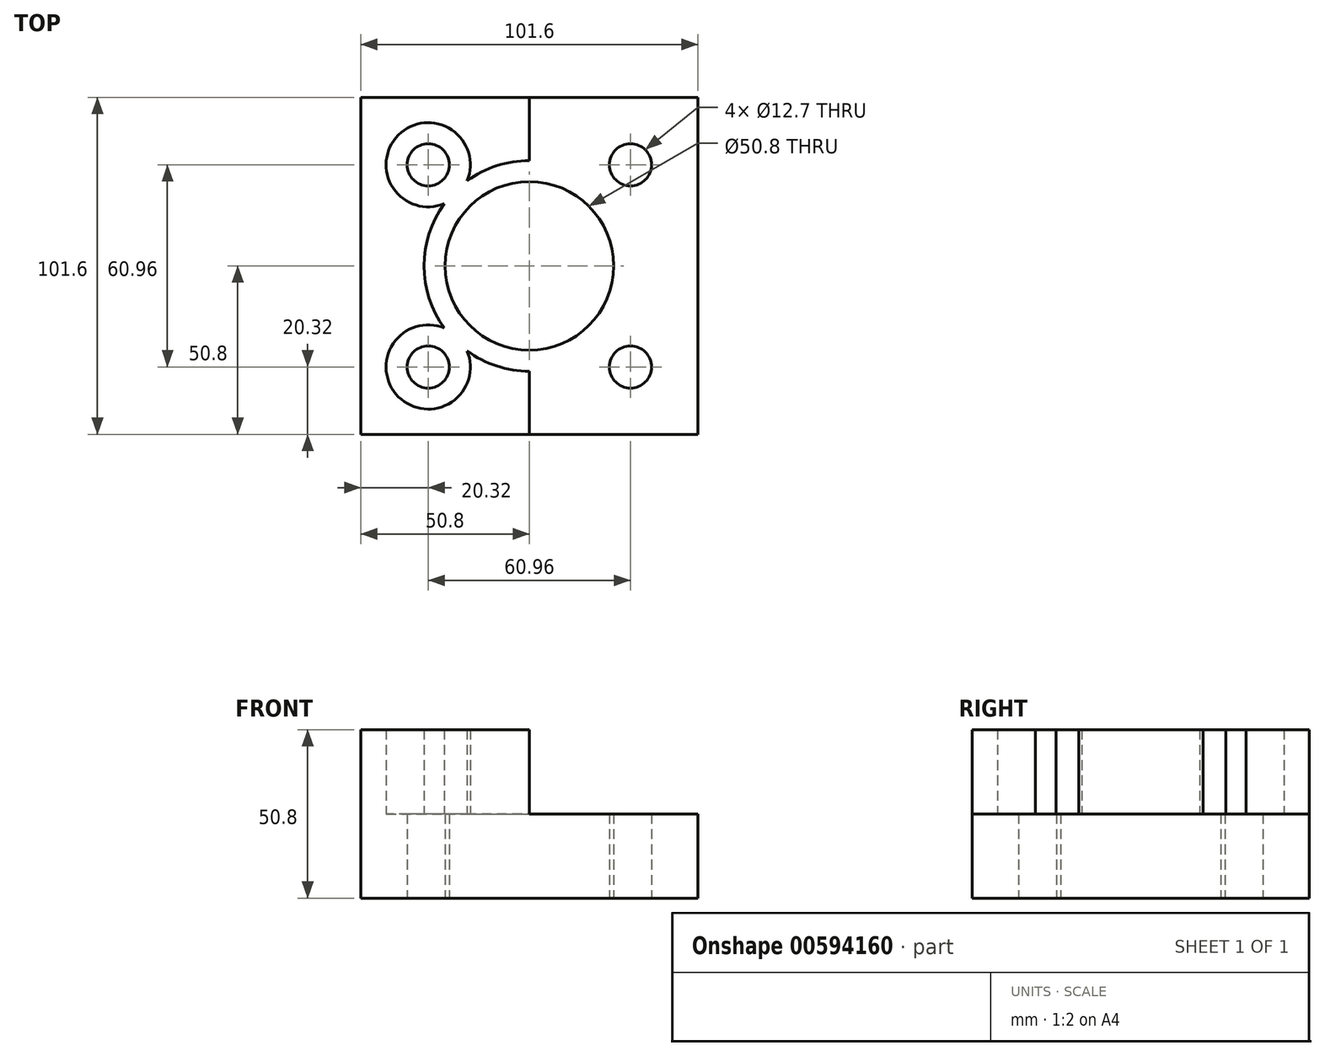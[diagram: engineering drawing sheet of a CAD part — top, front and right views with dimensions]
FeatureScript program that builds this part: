
annotation { "Feature Type Name" : "Feature", "Feature Type Description" : "" }
export const myFeature = defineFeature(function(context is Context, id is Id, definition is map)
    precondition{}
    {
        {
            var Q0;
            Q0=qCreatedBy(makeId("Top.planeOp"),FACE);
            var sketch = newSketch(context, id + "F0", { "sketchPlane" : qUnion([Q0])});
            skCircle(sketch, "E0", {"center": v(0, 0) * mm, "radius": 25.4 * mm});
            skLineSegment(sketch, "E1.bottom", {"start": v(-50.8, 50.8) * mm, "end": v(50.8, 50.8) * mm});
            skLineSegment(sketch, "E1.top", {"start": v(-50.8, -50.8) * mm, "end": v(50.8, -50.8) * mm});
            skLineSegment(sketch, "E1.left", {"start": v(-50.8, 50.8) * mm, "end": v(-50.8, -50.8) * mm});
            skLineSegment(sketch, "E1.right", {"start": v(50.8, 50.8) * mm, "end": v(50.8, -50.8) * mm});
            skCircle(sketch, "E2", {"center": v(-30.48, -30.48) * mm, "radius": 6.35 * mm});
            skCircle(sketch, "E3.1.0", {"center": v(30.48, -30.48) * mm, "radius": 6.35 * mm});
            skCircle(sketch, "E3.2.0", {"center": v(30.48, 30.48) * mm, "radius": 6.35 * mm});
            skCircle(sketch, "E3.3.0", {"center": v(-30.48, 30.48) * mm, "radius": 6.35 * mm});
            skSolve(sketch);
        }
        {
            var Q0;
            Q0 = qSketchRegion(id + "F0", true);
            extrude(context, id + "F1", {"entities" : qUnion([Q0]), "depth" : 25.4 * mm, "offsetDistance" : 25.4 * mm});
        }
        {
            var Q0;
            Q0=makeQuery(id+"F1.opExtrude","CAP_FACE",FACE,{"disambiguationData":[OSD([sQuery(id+"F0.wireOp",EDGE,"E0"),sQuery(id+"F0.wireOp",EDGE,"E1.bottom"),sQuery(id+"F0.wireOp",EDGE,"E1.top"),sQuery(id+"F0.wireOp",EDGE,"E1.left"),sQuery(id+"F0.wireOp",EDGE,"E1.right"),sQuery(id+"F0.wireOp",EDGE,"E2"),sQuery(id+"F0.wireOp",EDGE,"E3.1.0"),sQuery(id+"F0.wireOp",EDGE,"E3.2.0"),sQuery(id+"F0.wireOp",EDGE,"E3.3.0")])],"isStart":false});
            var sketch = newSketch(context, id + "F2", { "sketchPlane" : qUnion([Q0])});
            skCircle(sketch, "E4", {"center": v(-30.48, 30.48) * mm, "radius": 12.7 * mm});
            skCircle(sketch, "E5", {"center": v(-30.48, -30.48) * mm, "radius": 12.7 * mm});
            skLineSegment(sketch, "E6.bottom", {"start": v(-50.8, 50.8) * mm, "end": v(0, 50.8) * mm});
            skLineSegment(sketch, "E6.top", {"start": v(-50.8, -50.8) * mm, "end": v(0, -50.8) * mm});
            skLineSegment(sketch, "E6.left", {"start": v(-50.8, 50.8) * mm, "end": v(-50.8, -50.8) * mm});
            skLineSegment(sketch, "E6.right", {"start": v(0, 50.8) * mm, "end": v(0, -50.8) * mm});
            skCircle(sketch, "E7", {"center": v(0, 0) * mm, "radius": 31.75 * mm});
            skSolve(sketch);
        }
        {
            var Q0;
            {var subQ6=sQuery(id+"F2.wireOp",EDGE,"E6.bottom");Q0=makeQuery(id+"F2.imprint","IMPRINT",FACE,{"disambiguationData":[TD([[makeQuery(id+"F2.imprint","IMPRINT",EDGE,{"derivedFrom":subQ6}),-1.0]])]});}
            extrude(context, id + "F3", {"entities" : qUnion([Q0]), "operationType" : NewBodyOperationType.ADD, "depth" : 25.4 * mm, "offsetDistance" : 25.4 * mm});
        }
    });
